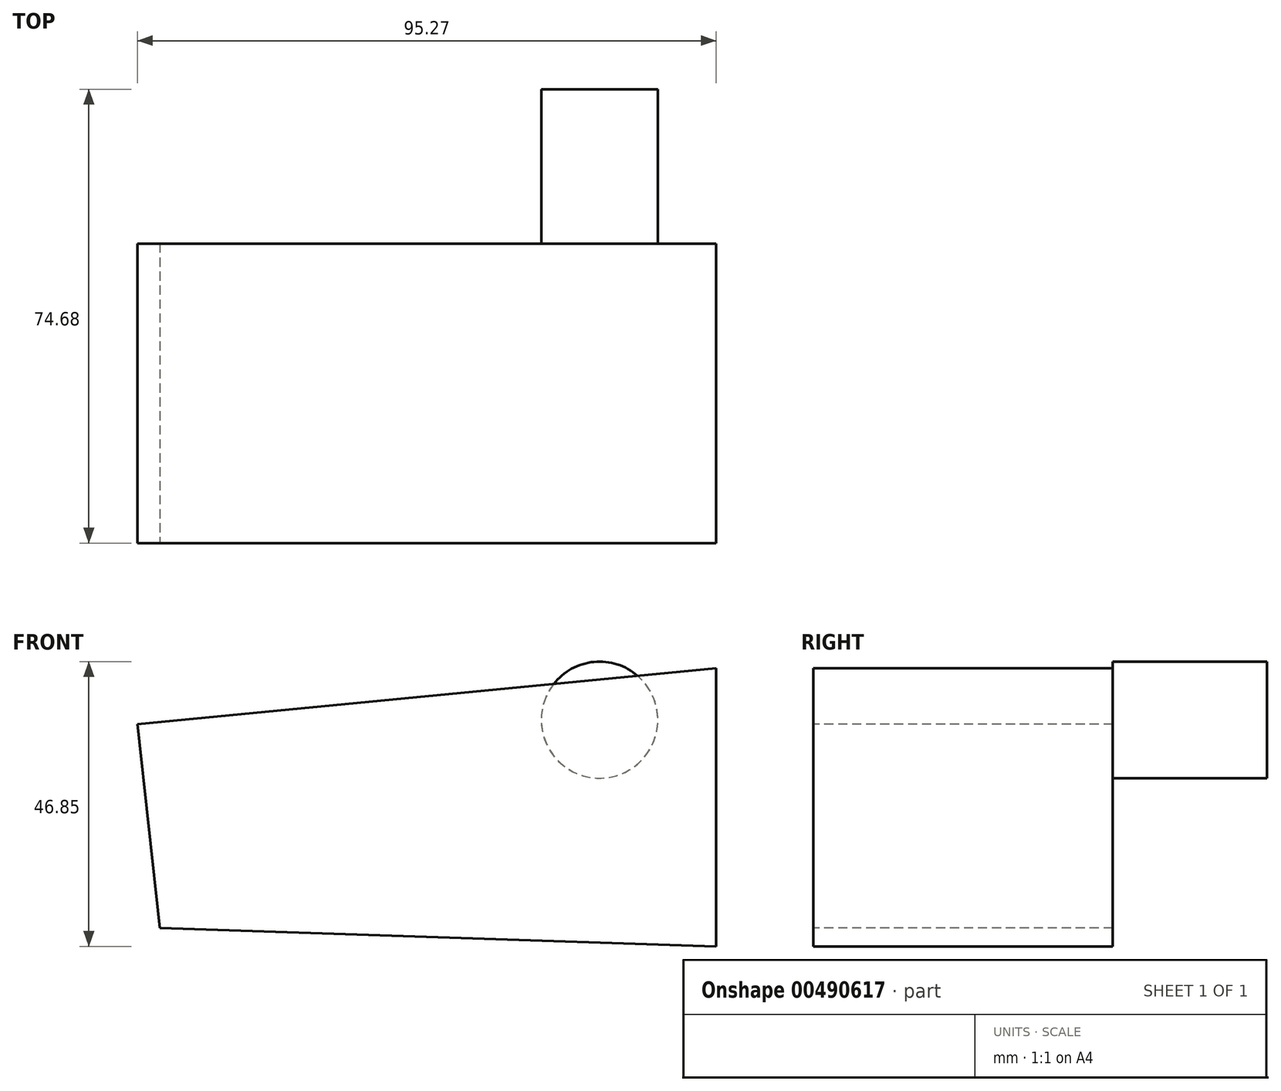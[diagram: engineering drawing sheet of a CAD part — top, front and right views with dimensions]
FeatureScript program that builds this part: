
annotation { "Feature Type Name" : "Feature", "Feature Type Description" : "" }
export const myFeature = defineFeature(function(context is Context, id is Id, definition is map)
    precondition{}
    {
        {
            var Q0;
            Q0=qCreatedBy(makeId("Front.planeOp"),FACE);
            var sketch = newSketch(context, id + "F0", { "sketchPlane" : qUnion([Q0])});
            skLineSegment(sketch, "E0", {"start": v(-52.72, 18.96) * mm, "end": v(42.55, 28.21) * mm});
            skLineSegment(sketch, "E1", {"start": v(42.55, 28.21) * mm, "end": v(42.55, -17.57) * mm});
            skLineSegment(sketch, "E2", {"start": v(42.55, -17.57) * mm, "end": v(-49.02, -14.57) * mm});
            skLineSegment(sketch, "E3", {"start": v(-49.02, -14.57) * mm, "end": v(-52.72, 18.96) * mm});
            skSolve(sketch);
        }
        {
            var Q0;
            Q0=makeQuery(id+"F0.imprint","IMPRINT",FACE,{"disambiguationData":[TD([[makeQuery(id+"F0.imprint","IMPRINT",EDGE,{"derivedFrom":sQuery(id+"F0.wireOp",EDGE,"E0")}),-1.0]])]});
            extrude(context, id + "F1", {"entities" : qUnion([Q0]), "oppositeDirection" : true, "depth" : 49.28 * mm});
        }
        {
            var Q0;
            Q0=makeQuery(id+"F1.opExtrude","CAP_FACE",FACE,{"disambiguationData":[OSD([sQuery(id+"F0.wireOp",EDGE,"E0"),sQuery(id+"F0.wireOp",EDGE,"E1"),sQuery(id+"F0.wireOp",EDGE,"E2"),sQuery(id+"F0.wireOp",EDGE,"E3")])],"isStart":false});
            var sketch = newSketch(context, id + "F2", { "sketchPlane" : qUnion([Q0])});
            skCircle(sketch, "E4", {"center": v(-23.34, 19.69) * mm, "radius": 9.59 * mm});
            skSolve(sketch);
        }
        {
            var Q0;
            Q0 = qSketchRegion(id + "F2", true);
            extrude(context, id + "F3", {"entities" : qUnion([Q0]), "operationType" : NewBodyOperationType.ADD, "depth" : 25.4 * mm});
        }
    });
